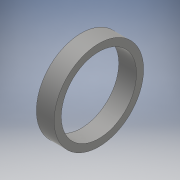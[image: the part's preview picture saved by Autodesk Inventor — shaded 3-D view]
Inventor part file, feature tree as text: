
AUTODESK INVENTOR PART (.ipt)
format: ipt  version: 2018 (Build 220112000, 112)  size: 103,424 bytes
history: native  units: mm
features: extrude x1, sketch x1
ambient origin geometry x8: Origin, YZ Plane, XZ Plane, XY Plane, X Axis, Y Axis, Z Axis, Center Point
bodies: Solid1 (feature_tree)
feature tree (2):
  extrude  "Extrusion1"  Depth=10.0mm
  sketch  "Sketch1"  dims[d0=42.418mm d2=4.0mm d3=10.0mm d4=0.0mm]
